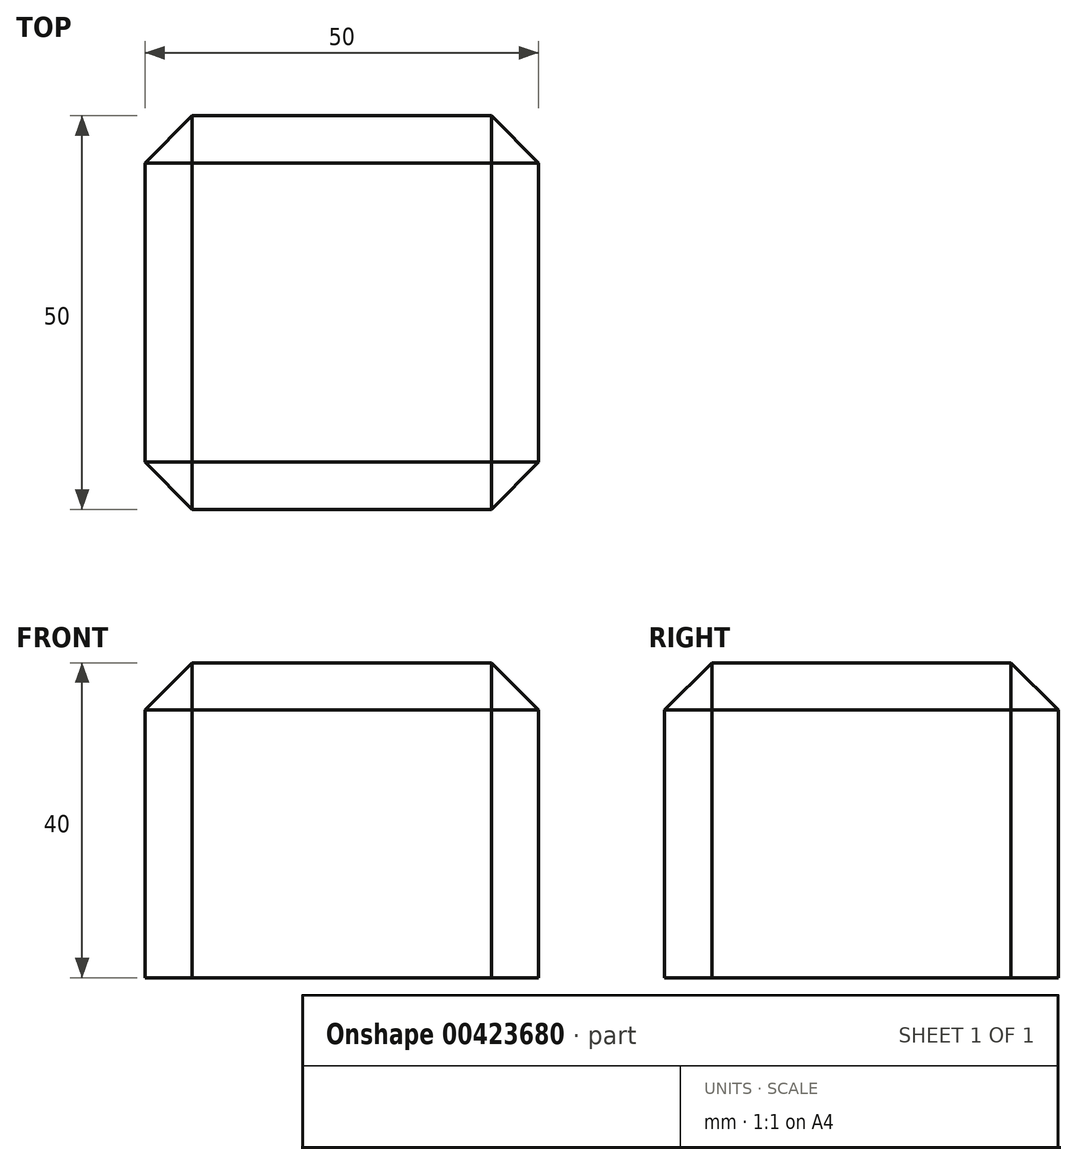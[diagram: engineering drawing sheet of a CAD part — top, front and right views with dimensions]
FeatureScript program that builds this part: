
annotation { "Feature Type Name" : "Feature", "Feature Type Description" : "" }
export const myFeature = defineFeature(function(context is Context, id is Id, definition is map)
    precondition{}
    {
        {
            var Q0;
            Q0=qCreatedBy(makeId("Top.planeOp"),FACE);
            var sketch = newSketch(context, id + "F0", { "sketchPlane" : qUnion([Q0])});
            skLineSegment(sketch, "E0.bottom", {"start": v(25, 25) * mm, "end": v(-25, 25) * mm});
            skLineSegment(sketch, "E0.top", {"start": v(25, -25) * mm, "end": v(-25, -25) * mm});
            skLineSegment(sketch, "E0.left", {"start": v(25, 25) * mm, "end": v(25, -25) * mm});
            skLineSegment(sketch, "E0.right", {"start": v(-25, 25) * mm, "end": v(-25, -25) * mm});
            skPoint(sketch, "E0.middle", {"position": v(0, 0) * mm});
            skSolve(sketch);
        }
        {
            var Q0;
            Q0=makeQuery(id+"F0.imprint","IMPRINT",FACE,{"disambiguationData":[TD([[makeQuery(id+"F0.imprint","IMPRINT",EDGE,{"derivedFrom":sQuery(id+"F0.wireOp",EDGE,"E0.bottom")}),1.0]])]});
            extrude(context, id + "F1", {"entities" : qUnion([Q0]), "depth" : 40 * mm});
        }
        {
            var Q0;
            Q0=makeQuery(id+"F1.opExtrude","CAP_EDGE",EDGE,{"disambiguationData":[OSD([sQuery(id+"F0.wireOp",EDGE,"E0.top")])],"isStart":false});
            var Q1;
            Q1=makeQuery(id+"F1.opExtrude","CAP_EDGE",EDGE,{"disambiguationData":[OSD([sQuery(id+"F0.wireOp",EDGE,"E0.left")])],"isStart":false});
            var Q2;
            Q2=makeQuery(id+"F1.opExtrude","CAP_EDGE",EDGE,{"disambiguationData":[OSD([sQuery(id+"F0.wireOp",EDGE,"E0.bottom")])],"isStart":false});
            var Q3;
            Q3=makeQuery(id+"F1.opExtrude","CAP_EDGE",EDGE,{"disambiguationData":[OSD([sQuery(id+"F0.wireOp",EDGE,"E0.right")])],"isStart":false});
            var Q4;
            Q4=makeQuery(id+"F1.opExtrude","SWEPT_EDGE",EDGE,{"disambiguationData":[OSD([sQuery(id+"F0.wireOp",EDGE,"E0.top"),sQuery(id+"F0.wireOp",EDGE,"E0.left")])]});
            var Q5;
            Q5=makeQuery(id+"F1.opExtrude","SWEPT_EDGE",EDGE,{"disambiguationData":[OSD([sQuery(id+"F0.wireOp",EDGE,"E0.bottom"),sQuery(id+"F0.wireOp",EDGE,"E0.left")])]});
            var Q6;
            Q6=makeQuery(id+"F1.opExtrude","SWEPT_EDGE",EDGE,{"disambiguationData":[OSD([sQuery(id+"F0.wireOp",EDGE,"E0.top"),sQuery(id+"F0.wireOp",EDGE,"E0.right")])]});
            var Q7;
            Q7=makeQuery(id+"F1.opExtrude","SWEPT_EDGE",EDGE,{"disambiguationData":[OSD([sQuery(id+"F0.wireOp",EDGE,"E0.bottom"),sQuery(id+"F0.wireOp",EDGE,"E0.right")])]});
            chamfer(context, id + "F2", {"entities" : qUnion([Q0, Q1, Q2, Q3, Q4, Q5, Q6, Q7]), "width" : 6 * mm, "tangentPropagation" : true});
        }
    });
